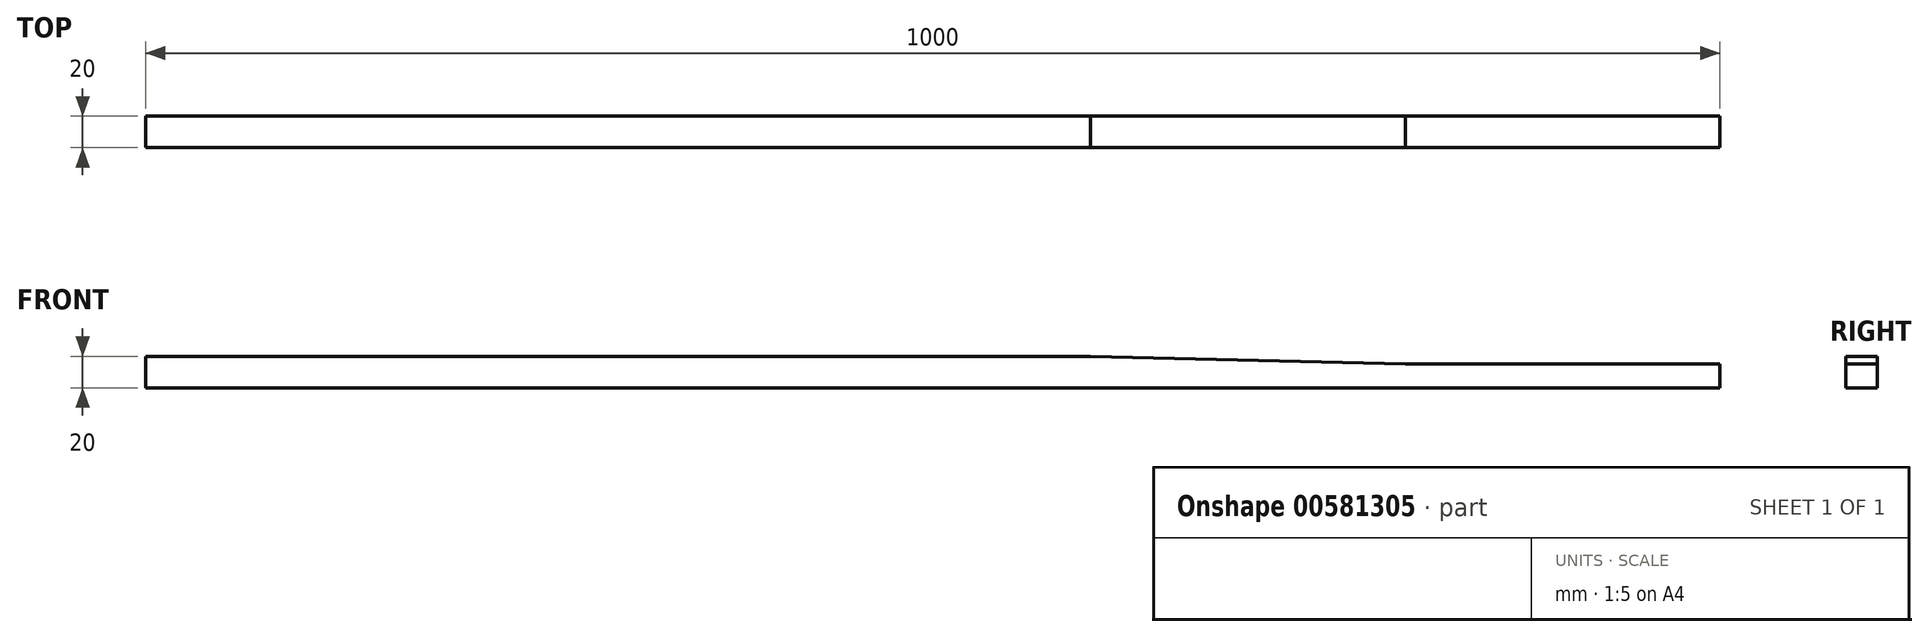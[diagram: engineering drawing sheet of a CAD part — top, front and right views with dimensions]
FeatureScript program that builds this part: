
annotation { "Feature Type Name" : "Feature", "Feature Type Description" : "" }
export const myFeature = defineFeature(function(context is Context, id is Id, definition is map)
    precondition{}
    {
        {
            var Q0;
            Q0=qCreatedBy(makeId("Front.planeOp"),FACE);
            var sketch = newSketch(context, id + "F0", { "sketchPlane" : qUnion([Q0])});
            skLineSegment(sketch, "E0", {"start": v(-112.06, 29.96) * mm, "end": v(487.94, 29.96) * mm});
            skLineSegment(sketch, "E1", {"start": v(487.94, 29.96) * mm, "end": v(687.94, 24.96) * mm});
            skLineSegment(sketch, "E2", {"start": v(687.94, 24.96) * mm, "end": v(887.94, 24.96) * mm});
            skLineSegment(sketch, "E3", {"start": v(887.94, 24.96) * mm, "end": v(887.94, 9.96) * mm});
            skLineSegment(sketch, "E4", {"start": v(887.94, 9.96) * mm, "end": v(-112.06, 9.96) * mm});
            skLineSegment(sketch, "E5", {"start": v(-112.06, 9.96) * mm, "end": v(-112.06, 29.96) * mm});
            skSolve(sketch);
        }
        {
            var Q0;
            Q0=makeQuery(id+"F0.imprint","IMPRINT",FACE,{"disambiguationData":[TD([[makeQuery(id+"F0.imprint","IMPRINT",EDGE,{"derivedFrom":sQuery(id+"F0.wireOp",EDGE,"E0")}),-1.0]])]});
            extrude(context, id + "F1", {"entities" : qUnion([Q0]), "depth" : 20 * mm, "offsetDistance" : 25 * mm});
        }
    });
